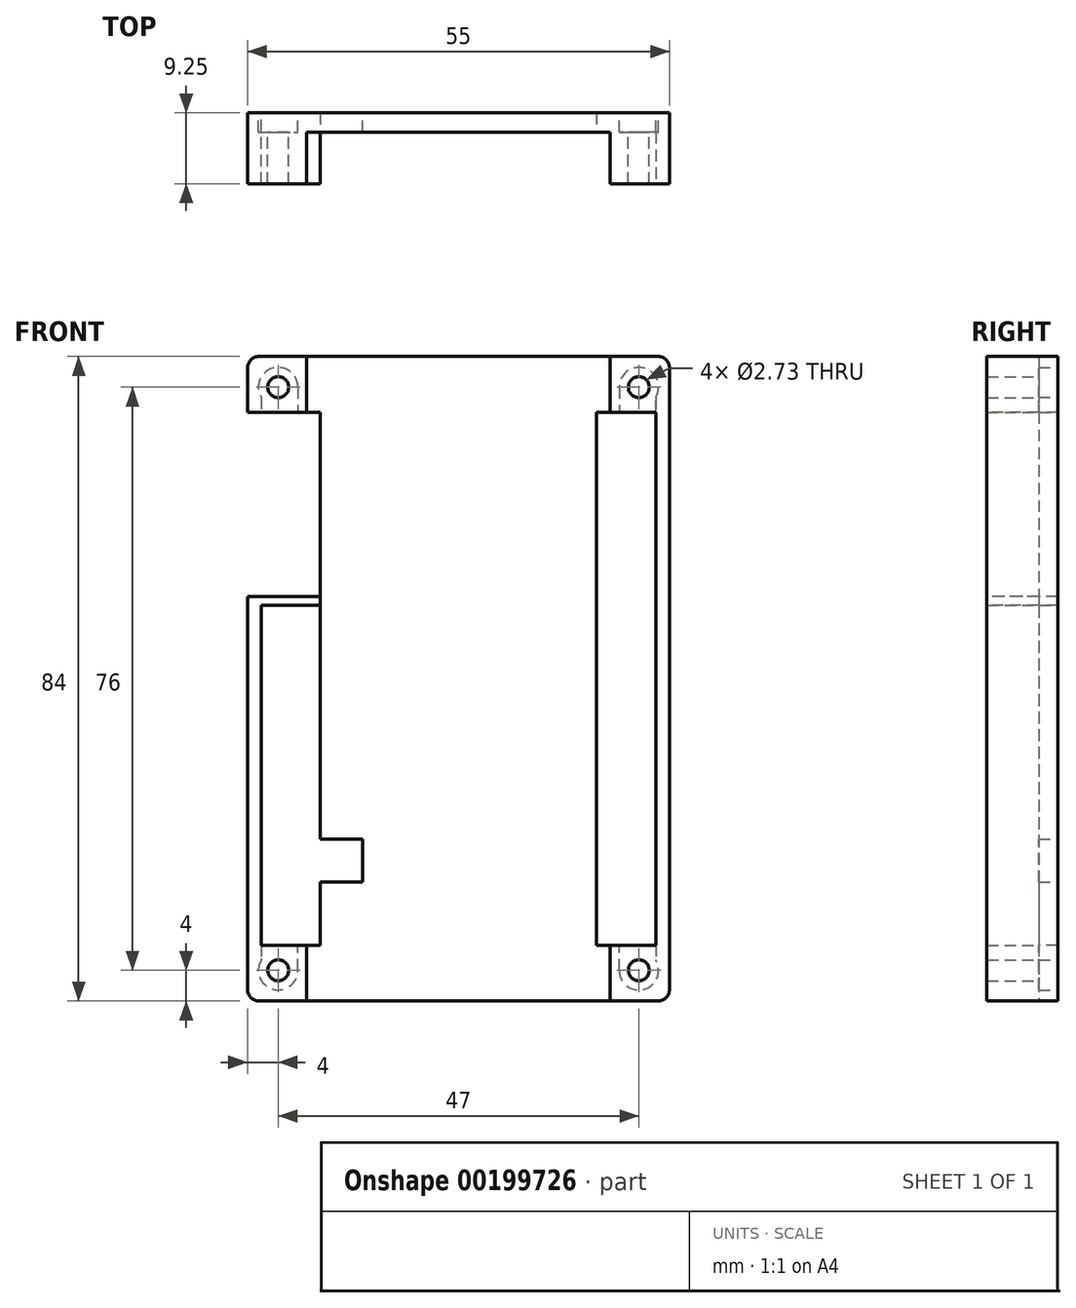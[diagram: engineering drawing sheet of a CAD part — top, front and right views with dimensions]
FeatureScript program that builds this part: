
annotation { "Feature Type Name" : "Feature", "Feature Type Description" : "" }
export const myFeature = defineFeature(function(context is Context, id is Id, definition is map)
    precondition{}
    {
        {
            var Q0;
            Q0=qCreatedBy(makeId("Front.planeOp"),FACE);
            var sketch = newSketch(context, id + "F0", { "sketchPlane" : qUnion([Q0])});
            skLineSegment(sketch, "E0.bottom", {"start": v(0, 0) * mm, "end": v(55, 0) * mm});
            skLineSegment(sketch, "E0.top", {"start": v(0, 84) * mm, "end": v(55, 84) * mm});
            skLineSegment(sketch, "E0.left", {"start": v(0, 0) * mm, "end": v(0, 84) * mm});
            skLineSegment(sketch, "E0.right", {"start": v(55, 0) * mm, "end": v(55, 84) * mm});
            skCircle(sketch, "E1", {"center": v(4, 80) * mm, "radius": 1.36 * mm});
            skCircle(sketch, "E2.0.1.0", {"center": v(4, 4) * mm, "radius": 1.36 * mm});
            skCircle(sketch, "E2.1.0.0", {"center": v(51, 80) * mm, "radius": 1.36 * mm});
            skCircle(sketch, "E2.1.1.0", {"center": v(51, 4) * mm, "radius": 1.36 * mm});
            skLineSegment(sketch, "E2.direction1", {"start": v(4, 80) * mm, "end": v(51, 80) * mm, "construction": true});
            skLineSegment(sketch, "E2.direction2", {"start": v(4, 80) * mm, "end": v(4, 4) * mm, "construction": true});
            skSolve(sketch);
        }
        {
            var Q0;
            Q0 = qSketchRegion(id + "F0", true);
            extrude(context, id + "F1", {"entities" : qUnion([Q0]), "depth" : 9.25 * mm});
        }
        {
            var Q0;
            Q0=makeQuery(id+"F1.opExtrude","CAP_FACE",FACE,{"disambiguationData":[OSD([sQuery(id+"F0.wireOp",EDGE,"E0.bottom"),sQuery(id+"F0.wireOp",EDGE,"E0.top"),sQuery(id+"F0.wireOp",EDGE,"E0.left"),sQuery(id+"F0.wireOp",EDGE,"E0.right"),sQuery(id+"F0.wireOp",EDGE,"E1"),sQuery(id+"F0.wireOp",EDGE,"E2.0.1.0"),sQuery(id+"F0.wireOp",EDGE,"E2.1.0.0"),sQuery(id+"F0.wireOp",EDGE,"E2.1.1.0")])],"isStart":false});
            var sketch = newSketch(context, id + "F2", { "sketchPlane" : qUnion([Q0])});
            skLineSegment(sketch, "E3.top", {"start": v(0, 76.74) * mm, "end": v(7.72, 76.74) * mm});
            skLineSegment(sketch, "E3.right", {"start": v(7.72, 84) * mm, "end": v(7.72, 76.74) * mm});
            skLineSegment(sketch, "E4.0.1.1", {"start": v(0, 7.26) * mm, "end": v(0, 0) * mm});
            skLineSegment(sketch, "E4.0.1.2", {"start": v(0, 7.26) * mm, "end": v(7.72, 7.26) * mm});
            skLineSegment(sketch, "E4.0.1.3", {"start": v(7.72, 7.26) * mm, "end": v(7.72, 0) * mm});
            skLineSegment(sketch, "E4.1.0.0", {"start": v(47.28, 76.74) * mm, "end": v(55, 76.74) * mm});
            skLineSegment(sketch, "E4.1.0.1", {"start": v(47.28, 84) * mm, "end": v(47.28, 76.74) * mm});
            skLineSegment(sketch, "E4.1.1.1", {"start": v(47.28, 7.26) * mm, "end": v(47.28, 0) * mm});
            skLineSegment(sketch, "E4.1.1.2", {"start": v(47.28, 7.26) * mm, "end": v(55, 7.26) * mm});
            skLineSegment(sketch, "E4.direction1", {"start": v(0, 76.74) * mm, "end": v(47.28, 76.74) * mm, "construction": true});
            skLineSegment(sketch, "E4.direction2", {"start": v(0, 76.74) * mm, "end": v(0, 7.26) * mm, "construction": true});
            skLineSegment(sketch, "E5", {"start": v(0, 76.74) * mm, "end": v(0, 7.26) * mm});
            skLineSegment(sketch, "E6", {"start": v(7.72, 0) * mm, "end": v(47.28, 0) * mm});
            skLineSegment(sketch, "E7", {"start": v(55, 7.26) * mm, "end": v(55, 76.74) * mm});
            skLineSegment(sketch, "E8", {"start": v(47.28, 84) * mm, "end": v(7.72, 84) * mm});
            skSolve(sketch);
        }
        {
            var Q0;
            Q0 = qSketchRegion(id + "F2", true);
            extrude(context, id + "F3", {"entities" : qUnion([Q0]), "operationType" : NewBodyOperationType.REMOVE, "oppositeDirection" : true, "depth" : 6.75 * mm});
        }
        {
            var Q0;
            Q0=makeQuery(id+"F3.boolean.opBoolean","COPY",FACE,{"derivedFrom":makeQuery(id+"F3.opExtrude","CAP_FACE",FACE,{"disambiguationData":[OSD([sQuery(id+"F2.wireOp",EDGE,"E3.top"),sQuery(id+"F2.wireOp",EDGE,"E3.right"),sQuery(id+"F2.wireOp",EDGE,"E4.0.1.2"),sQuery(id+"F2.wireOp",EDGE,"E4.0.1.3"),sQuery(id+"F2.wireOp",EDGE,"E4.1.0.0"),sQuery(id+"F2.wireOp",EDGE,"E4.1.0.1"),sQuery(id+"F2.wireOp",EDGE,"E4.1.1.1"),sQuery(id+"F2.wireOp",EDGE,"E4.1.1.2"),sQuery(id+"F2.wireOp",EDGE,"E5"),sQuery(id+"F2.wireOp",EDGE,"E6"),sQuery(id+"F2.wireOp",EDGE,"E7"),sQuery(id+"F2.wireOp",EDGE,"E8")])],"isStart":false})});
            var sketch = newSketch(context, id + "F4", { "sketchPlane" : qUnion([Q0])});
            skLineSegment(sketch, "E9.bottom", {"start": v(1.8, 76.74) * mm, "end": v(9.5, 76.74) * mm});
            skLineSegment(sketch, "E9.top", {"start": v(1.8, 7.26) * mm, "end": v(9.5, 7.26) * mm});
            skLineSegment(sketch, "E9.left", {"start": v(1.8, 76.74) * mm, "end": v(1.8, 7.26) * mm});
            skLineSegment(sketch, "E9.right", {"start": v(9.5, 76.74) * mm, "end": v(9.5, 7.26) * mm});
            skLineSegment(sketch, "E10.bottom", {"start": v(45.5, 76.74) * mm, "end": v(53.2, 76.74) * mm});
            skLineSegment(sketch, "E10.top", {"start": v(45.5, 7.26) * mm, "end": v(53.2, 7.26) * mm});
            skLineSegment(sketch, "E10.left", {"start": v(45.5, 76.74) * mm, "end": v(45.5, 7.26) * mm});
            skLineSegment(sketch, "E10.right", {"start": v(53.2, 76.74) * mm, "end": v(53.2, 7.26) * mm});
            skSolve(sketch);
        }
        {
            var Q0;
            Q0 = qSketchRegion(id + "F4", true);
            extrude(context, id + "F5", {"entities" : qUnion([Q0]), "operationType" : NewBodyOperationType.REMOVE, "endBound" : BoundingType.THROUGH_ALL, "oppositeDirection" : true, "depth" : 25 * mm});
        }
        {
            var Q0;
            Q0=makeQuery(id+"F1.opExtrude","CAP_FACE",FACE,{"disambiguationData":[OSD([sQuery(id+"F0.wireOp",EDGE,"E0.bottom"),sQuery(id+"F0.wireOp",EDGE,"E0.top"),sQuery(id+"F0.wireOp",EDGE,"E0.left"),sQuery(id+"F0.wireOp",EDGE,"E0.right"),sQuery(id+"F0.wireOp",EDGE,"E1"),sQuery(id+"F0.wireOp",EDGE,"E2.0.1.0"),sQuery(id+"F0.wireOp",EDGE,"E2.1.0.0"),sQuery(id+"F0.wireOp",EDGE,"E2.1.1.0")])],"isStart":true});
            var sketch = newSketch(context, id + "F6", { "sketchPlane" : qUnion([Q0])});
            skArc(sketch, "E11", {"start": v(-53.2, 5.33) * mm, "mid": v(-51.69, 1.52) * mm, "end": v(-48.43, 4) * mm});
            skArc(sketch, "E12.0.1.0", {"start": v(-48.43, 80) * mm, "mid": v(-51.69, 82.48) * mm, "end": v(-53.2, 78.67) * mm});
            skArc(sketch, "E12.1.0.0", {"start": v(-6.57, 4) * mm, "mid": v(-3.31, 1.52) * mm, "end": v(-1.8, 5.33) * mm});
            skArc(sketch, "E12.1.1.0", {"start": v(-1.8, 78.67) * mm, "mid": v(-3.31, 82.48) * mm, "end": v(-6.57, 80) * mm});
            skLineSegment(sketch, "E12.direction1", {"start": v(-51, 4) * mm, "end": v(-4, 4) * mm, "construction": true});
            skLineSegment(sketch, "E12.direction2", {"start": v(-51, 4) * mm, "end": v(-51, 80) * mm, "construction": true});
            skLineSegment(sketch, "E13", {"start": v(-53.2, 7.26) * mm, "end": v(-53.2, 5.33) * mm});
            skLineSegment(sketch, "E14", {"start": v(-48.43, 4) * mm, "end": v(-48.43, 7.26) * mm});
            skLineSegment(sketch, "E15", {"start": v(-53.2, 7.26) * mm, "end": v(-48.43, 7.26) * mm});
            skLineSegment(sketch, "E16", {"start": v(-1.8, 7.26) * mm, "end": v(-1.8, 5.33) * mm});
            skLineSegment(sketch, "E17", {"start": v(-6.57, 4) * mm, "end": v(-6.57, 7.26) * mm});
            skLineSegment(sketch, "E18", {"start": v(-1.8, 76.74) * mm, "end": v(-1.8, 78.67) * mm});
            skLineSegment(sketch, "E19", {"start": v(-6.57, 80) * mm, "end": v(-6.57, 76.74) * mm});
            skLineSegment(sketch, "E20", {"start": v(-53.2, 76.74) * mm, "end": v(-53.2, 78.67) * mm});
            skLineSegment(sketch, "E21", {"start": v(-48.43, 80) * mm, "end": v(-48.43, 76.74) * mm});
            skLineSegment(sketch, "E22", {"start": v(-48.43, 76.74) * mm, "end": v(-53.2, 76.74) * mm});
            skLineSegment(sketch, "E23", {"start": v(-6.57, 76.74) * mm, "end": v(-1.8, 76.74) * mm});
            skLineSegment(sketch, "E24", {"start": v(-6.57, 7.26) * mm, "end": v(-1.8, 7.26) * mm});
            skSolve(sketch);
        }
        {
            var Q0;
            Q0 = qSketchRegion(id + "F6", true);
            extrude(context, id + "F7", {"entities" : qUnion([Q0]), "operationType" : NewBodyOperationType.REMOVE, "oppositeDirection" : true, "depth" : 2.5 * mm});
        }
        {
            var Q0;
            Q0=makeQuery(id+"F5.boolean.opBoolean","MERGE",FACE,{"derivedFrom":[makeQuery(id+"F3.boolean.opBoolean","COPY",FACE,{"derivedFrom":makeQuery(id+"F3.opExtrude","SWEPT_FACE",FACE,{"disambiguationData":[OSD([sQuery(id+"F2.wireOp",EDGE,"E4.0.1.2")])]})}),makeQuery(id+"F5.opExtrude","SWEPT_FACE",FACE,{"disambiguationData":[OSD([sQuery(id+"F4.wireOp",EDGE,"E9.top")])]})]});
            var sketch = newSketch(context, id + "F8", { "sketchPlane" : qUnion([Q0])});
            skLineSegment(sketch, "E25", {"start": v(1.8, -2.5) * mm, "end": v(0, -2.5) * mm});
            skLineSegment(sketch, "E26", {"start": v(0, -2.5) * mm, "end": v(0, -9.25) * mm});
            skLineSegment(sketch, "E27", {"start": v(0, -9.25) * mm, "end": v(1.8, -9.25) * mm});
            skLineSegment(sketch, "E28", {"start": v(1.8, -9.25) * mm, "end": v(1.8, -2.5) * mm});
            skLineSegment(sketch, "E29", {"start": v(55, -2.5) * mm, "end": v(55, -9.25) * mm});
            skPoint(sketch, "E29.startSnap0", {"position": v(0.9, -2.5) * mm});
            skLineSegment(sketch, "E30", {"start": v(55, -2.5) * mm, "end": v(53.2, -2.5) * mm});
            skLineSegment(sketch, "E31", {"start": v(53.2, -2.5) * mm, "end": v(53.2, -9.25) * mm});
            skLineSegment(sketch, "E32", {"start": v(53.2, -9.25) * mm, "end": v(55, -9.25) * mm});
            skSolve(sketch);
        }
        {
            var Q0;
            Q0 = qSketchRegion(id + "F8", true);
            extrude(context, id + "F9", {"entities" : qUnion([Q0]), "operationType" : NewBodyOperationType.ADD, "depth" : (84 - 7.72) * mm});
        }
        {
            var Q0;
            Q0=makeQuery(id+"F1.opExtrude","CAP_FACE",FACE,{"disambiguationData":[OSD([sQuery(id+"F0.wireOp",EDGE,"E0.bottom"),sQuery(id+"F0.wireOp",EDGE,"E0.top"),sQuery(id+"F0.wireOp",EDGE,"E0.left"),sQuery(id+"F0.wireOp",EDGE,"E0.right"),sQuery(id+"F0.wireOp",EDGE,"E1"),sQuery(id+"F0.wireOp",EDGE,"E2.0.1.0"),sQuery(id+"F0.wireOp",EDGE,"E2.1.0.0"),sQuery(id+"F0.wireOp",EDGE,"E2.1.1.0")])],"isStart":true});
            var sketch = newSketch(context, id + "F10", { "sketchPlane" : qUnion([Q0])});
            skLineSegment(sketch, "E33.bottom", {"start": v(-1.8, 76.74) * mm, "end": v(0, 76.74) * mm});
            skLineSegment(sketch, "E33.top", {"start": v(-1.8, 51.54) * mm, "end": v(0, 51.54) * mm});
            skLineSegment(sketch, "E33.left", {"start": v(-1.8, 76.74) * mm, "end": v(-1.8, 51.54) * mm});
            skLineSegment(sketch, "E33.right", {"start": v(0, 76.74) * mm, "end": v(0, 51.54) * mm});
            skSolve(sketch);
        }
        {
            var Q0;
            Q0 = qSketchRegion(id + "F10", true);
            extrude(context, id + "F11", {"entities" : qUnion([Q0]), "operationType" : NewBodyOperationType.REMOVE, "endBound" : BoundingType.THROUGH_ALL, "oppositeDirection" : true, "depth" : 25 * mm});
        }
        {
            var Q0;
            Q0=makeQuery(id+"F1.opExtrude","SWEPT_EDGE",EDGE,{"disambiguationData":[OSD([sQuery(id+"F0.wireOp",EDGE,"E0.top"),sQuery(id+"F0.wireOp",EDGE,"E0.right")])]});
            var Q1;
            Q1=makeQuery(id+"F1.opExtrude","SWEPT_EDGE",EDGE,{"disambiguationData":[OSD([sQuery(id+"F0.wireOp",EDGE,"E0.bottom"),sQuery(id+"F0.wireOp",EDGE,"E0.right")])]});
            var Q2;
            Q2=makeQuery(id+"F1.opExtrude","SWEPT_EDGE",EDGE,{"disambiguationData":[OSD([sQuery(id+"F0.wireOp",EDGE,"E0.top"),sQuery(id+"F0.wireOp",EDGE,"E0.left")])]});
            var Q3;
            Q3=makeQuery(id+"F1.opExtrude","SWEPT_EDGE",EDGE,{"disambiguationData":[OSD([sQuery(id+"F0.wireOp",EDGE,"E0.bottom"),sQuery(id+"F0.wireOp",EDGE,"E0.left")])]});
            fillet(context, id + "F12", {"entities" : qUnion([Q0, Q1, Q2, Q3]), "radius" : 1.5 * mm, "tangentPropagation" : true, "allowEdgeOverflow" : false});
        }
        {
            var Q0;
            Q0=makeQuery(id+"F72ecqpt5NNyPZf_1.boolean.opBoolean","MERGE",FACE,{"derivedFrom":[makeQuery(id+"F1.opExtrude","CAP_FACE",FACE,{"disambiguationData":[OSD([sQuery(id+"F0.wireOp",EDGE,"E0.bottom"),sQuery(id+"F0.wireOp",EDGE,"E0.top"),sQuery(id+"F0.wireOp",EDGE,"E0.left"),sQuery(id+"F0.wireOp",EDGE,"E0.right"),sQuery(id+"F0.wireOp",EDGE,"E1"),sQuery(id+"F0.wireOp",EDGE,"E2.0.1.0"),sQuery(id+"F0.wireOp",EDGE,"E2.1.0.0"),sQuery(id+"F0.wireOp",EDGE,"E2.1.1.0")])],"isStart":true}),makeQuery(id+"F72ecqpt5NNyPZf_1.opExtrude","SWEPT_FACE",FACE,{"disambiguationData":[OSD([sQuery(id+"FX5j2vnTi4zrZpc_1.wireOp",EDGE,"cY1L1arP-l40L-kX1V-mlM8-KhXmsw0WbdG4.left")])]})]});
            var sketch = newSketch(context, id + "F13", { "sketchPlane" : qUnion([Q0])});
            skLineSegment(sketch, "E34.bottom", {"start": v(-15, 15.5) * mm, "end": v(-11.28, 15.5) * mm});
            skLineSegment(sketch, "E34.top", {"start": v(-15, 21.07) * mm, "end": v(-11.28, 21.07) * mm});
            skLineSegment(sketch, "E34.left", {"start": v(-15, 21.07) * mm, "end": v(-15, 15.5) * mm});
            skLineSegment(sketch, "E35", {"start": v(-11.28, 15.5) * mm, "end": v(-9.5, 15.5) * mm});
            skLineSegment(sketch, "E36", {"start": v(-9.5, 15.5) * mm, "end": v(-9.5, 21.07) * mm});
            skLineSegment(sketch, "E37", {"start": v(-9.5, 21.07) * mm, "end": v(-11.28, 21.07) * mm});
            skSolve(sketch);
        }
        {
            var Q0;
            Q0 = qSketchRegion(id + "F13", true);
            extrude(context, id + "F14", {"entities" : qUnion([Q0]), "operationType" : NewBodyOperationType.REMOVE, "endBound" : BoundingType.THROUGH_ALL, "oppositeDirection" : true, "depth" : 25 * mm});
        }
        {
            var Q0;
            Q0=qCreatedBy(makeId("Right.planeOp"),FACE);
            var sketch = newSketch(context, id + "F15", { "sketchPlane" : qUnion([Q0])});
            skLineSegment(sketch, "E38.bottom", {"start": v(0, 51.54) * mm, "end": v(-9.25, 51.54) * mm});
            skLineSegment(sketch, "E38.top", {"start": v(0, 52.74) * mm, "end": v(-9.25, 52.74) * mm});
            skLineSegment(sketch, "E38.left", {"start": v(0, 51.54) * mm, "end": v(0, 52.74) * mm});
            skLineSegment(sketch, "E38.right", {"start": v(-9.25, 51.54) * mm, "end": v(-9.25, 52.74) * mm});
            skSolve(sketch);
        }
        {
            var Q0;
            Q0 = qSketchRegion(id + "F15", true);
            extrude(context, id + "F16", {"entities" : qUnion([Q0]), "operationType" : NewBodyOperationType.ADD, "depth" : 9.5 * mm});
        }
    });
